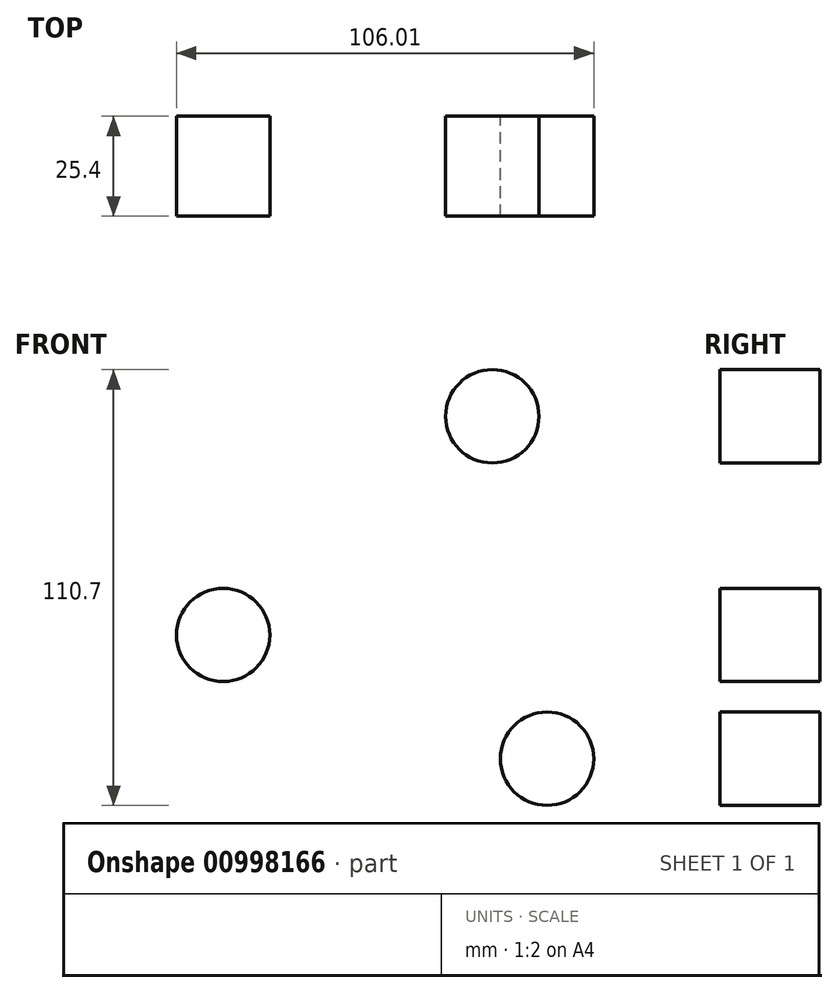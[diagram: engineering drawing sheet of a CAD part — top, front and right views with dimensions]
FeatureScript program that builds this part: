
annotation { "Feature Type Name" : "Feature", "Feature Type Description" : "" }
export const myFeature = defineFeature(function(context is Context, id is Id, definition is map)
    precondition{}
    {
        {
            var Q0;
            Q0=qCreatedBy(makeId("Front.planeOp"),FACE);
            var sketch = newSketch(context, id + "F0", { "sketchPlane" : qUnion([Q0])});
            skCircle(sketch, "E0", {"center": v(18.15, 47.52) * mm, "radius": 11.86 * mm});
            skCircle(sketch, "E1.1.0", {"center": v(-50.23, -8.04) * mm, "radius": 11.86 * mm});
            skCircle(sketch, "E1.2.0", {"center": v(32.08, -39.47) * mm, "radius": 11.86 * mm});
            skPoint(sketch, "E1.center", {"position": v(0, 0) * mm});
            skLineSegment(sketch, "E1.anchor1", {"start": v(0, 0) * mm, "end": v(18.15, 47.52) * mm, "construction": true});
            skLineSegment(sketch, "E1.anchor2", {"start": v(0, 0) * mm, "end": v(32.08, -39.47) * mm, "construction": true});
            skSolve(sketch);
        }
        {
            var Q0;
            Q0 = qSketchRegion(id + "F0", true);
            extrude(context, id + "F1", {"entities" : qUnion([Q0]), "depth" : 25.4 * mm, "offsetDistance" : 25.4 * mm});
        }
    });
